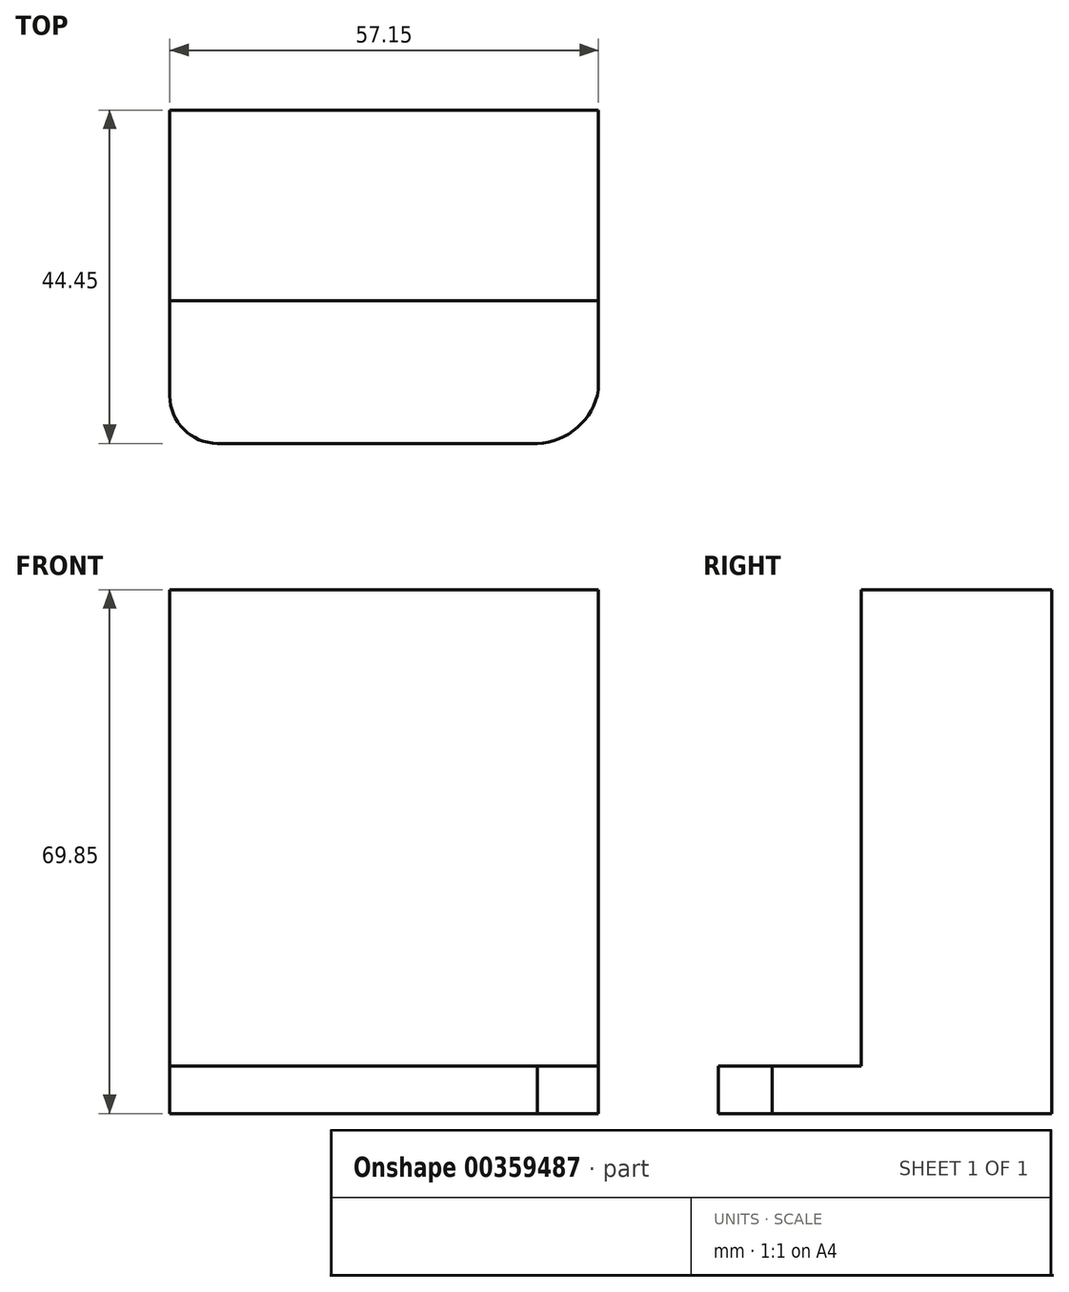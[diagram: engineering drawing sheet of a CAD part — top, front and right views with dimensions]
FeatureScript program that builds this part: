
annotation { "Feature Type Name" : "Feature", "Feature Type Description" : "" }
export const myFeature = defineFeature(function(context is Context, id is Id, definition is map)
    precondition{}
    {
        {
            var Q0;
            Q0=qCreatedBy(makeId("Front.planeOp"),FACE);
            var sketch = newSketch(context, id + "F0", { "sketchPlane" : qUnion([Q0])});
            skLineSegment(sketch, "E0", {"start": v(0, 69.85) * mm, "end": v(0, 0) * mm});
            skLineSegment(sketch, "E1", {"start": v(0, 0) * mm, "end": v(69.85, 0) * mm});
            skLineSegment(sketch, "E2", {"start": v(69.85, 0) * mm, "end": v(69.85, 69.85) * mm});
            skLineSegment(sketch, "E3", {"start": v(69.85, 69.85) * mm, "end": v(0, 69.85) * mm});
            skSolve(sketch);
        }
        {
            var Q0;
            Q0=makeQuery(id+"F0.imprint","IMPRINT",FACE,{"disambiguationData":[TD([[makeQuery(id+"F0.imprint","IMPRINT",EDGE,{"derivedFrom":sQuery(id+"F0.wireOp",EDGE,"E0")}),1.0]])]});
            extrude(context, id + "F1", {"entities" : qUnion([Q0]), "oppositeDirection" : true, "depth" : 44.45 * mm});
        }
        {
            var Q0;
            Q0=makeQuery(id+"F1.opExtrude","CAP_FACE",FACE,{"disambiguationData":[OSD([sQuery(id+"F0.wireOp",EDGE,"E0"),sQuery(id+"F0.wireOp",EDGE,"E1"),sQuery(id+"F0.wireOp",EDGE,"E2"),sQuery(id+"F0.wireOp",EDGE,"E3")])],"isStart":true});
            var sketch = newSketch(context, id + "F2", { "sketchPlane" : qUnion([Q0])});
            skLineSegment(sketch, "E4", {"start": v(0, 6.35) * mm, "end": v(69.85, 6.35) * mm});
            skLineSegment(sketch, "E5", {"start": v(69.85, 6.35) * mm, "end": v(69.85, 0) * mm});
            skLineSegment(sketch, "E6", {"start": v(69.85, 0) * mm, "end": v(0, 0) * mm});
            skLineSegment(sketch, "E7", {"start": v(0, 0) * mm, "end": v(0, 6.35) * mm});
            skSolve(sketch);
        }
        {
            var Q0;
            {var subQ0=sQuery(id+"F2.wireOp",EDGE,"E4");Q0=makeQuery(id+"F2.imprint","IMPRINT",FACE,{"disambiguationData":[TD([[makeQuery(id+"F2.imprint","IMPRINT",EDGE,{"derivedFrom":subQ0}),1.0]])]});}
            extrude(context, id + "F3", {"entities" : qUnion([Q0]), "operationType" : NewBodyOperationType.REMOVE, "oppositeDirection" : true, "depth" : 19.05 * mm});
        }
        {
            var Q0;
            Q0=qCreatedBy(makeId("Top.planeOp"),FACE);
            var sketch = newSketch(context, id + "F4", { "sketchPlane" : qUnion([Q0])});
            skLineSegment(sketch, "E8", {"start": v(48.99, 0) * mm, "end": v(69.85, 0) * mm});
            skLineSegment(sketch, "E9", {"start": v(69.85, 0) * mm, "end": v(69.85, 44.45) * mm});
            skLineSegment(sketch, "E10", {"start": v(69.85, 44.45) * mm, "end": v(57.15, 44.45) * mm});
            skLineSegment(sketch, "E11", {"start": v(57.15, 44.45) * mm, "end": v(57.15, 7.14) * mm});
            skArc(sketch, "E12", {"start": v(48.99, 0) * mm, "mid": v(54.34, 2.12) * mm, "end": v(57.15, 7.14) * mm});
            skSolve(sketch);
        }
        {
            var Q0;
            Q0 = qSketchRegion(id + "F4", true);
            extrude(context, id + "F5", {"entities" : qUnion([Q0]), "operationType" : NewBodyOperationType.REMOVE, "depth" : 69.85 * mm});
        }
        {
            var Q0;
            Q0=qCreatedBy(makeId("Top.planeOp"),FACE);
            var sketch = newSketch(context, id + "F6", { "sketchPlane" : qUnion([Q0])});
            skLineSegment(sketch, "E13", {"start": v(0, 6.35) * mm, "end": v(0, 0) * mm});
            skLineSegment(sketch, "E14", {"start": v(0, 0) * mm, "end": v(6.35, 0) * mm});
            skArc(sketch, "E15", {"start": v(0, 6.35) * mm, "mid": v(1.86, 1.86) * mm, "end": v(6.35, 0) * mm});
            skSolve(sketch);
        }
        {
            var Q0;
            Q0 = qSketchRegion(id + "F6", true);
            extrude(context, id + "F7", {"entities" : qUnion([Q0]), "operationType" : NewBodyOperationType.REMOVE, "depth" : 25.4 * mm});
        }
    });
